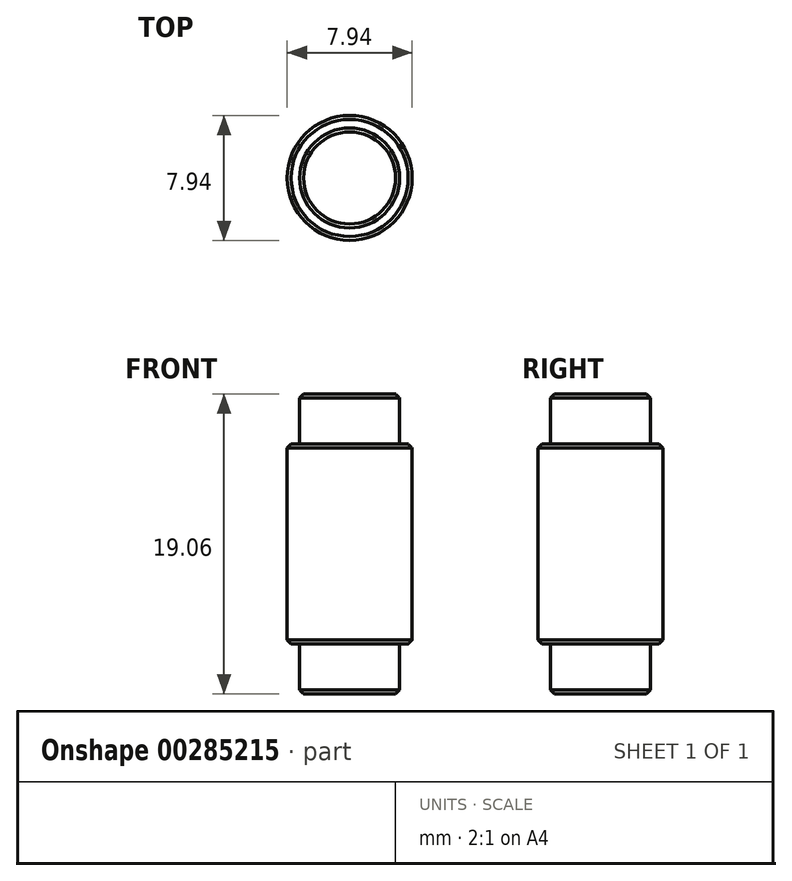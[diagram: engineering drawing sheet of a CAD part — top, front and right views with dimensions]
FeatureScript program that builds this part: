
annotation { "Feature Type Name" : "Feature", "Feature Type Description" : "" }
export const myFeature = defineFeature(function(context is Context, id is Id, definition is map)
    precondition{}
    {
        {
            var Q0;
            Q0=qCreatedBy(makeId("Top.planeOp"),FACE);
            var sketch = newSketch(context, id + "F0", { "sketchPlane" : qUnion([Q0])});
            skCircle(sketch, "E0", {"center": v(0, 0) * mm, "radius": 3.97 * mm});
            skSolve(sketch);
        }
        {
            var Q0;
            Q0 = qSketchRegion(id + "F0", true);
            extrude(context, id + "F1", {"entities" : qUnion([Q0]), "depth" : 12.7 * mm});
        }
        {
            var Q0;
            Q0=makeQuery(id+"F1.opExtrude","CAP_FACE",FACE,{"disambiguationData":[OSD([sQuery(id+"F0.wireOp",EDGE,"E0")])],"isStart":false});
            var sketch = newSketch(context, id + "F2", { "sketchPlane" : qUnion([Q0])});
            skCircle(sketch, "E1", {"center": v(0, 0) * mm, "radius": 3.18 * mm});
            skSolve(sketch);
        }
        {
            var Q0;
            Q0=makeQuery(id+"F2.imprint","IMPRINT",FACE,{"disambiguationData":[TD([[makeQuery(id+"F2.imprint","IMPRINT",EDGE,{"derivedFrom":sQuery(id+"F2.wireOp",EDGE,"E1")}),1.0]])]});
            extrude(context, id + "F3", {"entities" : qUnion([Q0]), "operationType" : NewBodyOperationType.ADD, "depth" : 3.17 * mm});
        }
        {
            var Q0;
            Q0=makeQuery(id+"F1.opExtrude","CAP_FACE",FACE,{"disambiguationData":[OSD([sQuery(id+"F0.wireOp",EDGE,"E0")])],"isStart":true});
            var sketch = newSketch(context, id + "F4", { "sketchPlane" : qUnion([Q0])});
            skCircle(sketch, "E2", {"center": v(0, 0) * mm, "radius": 3.18 * mm});
            skSolve(sketch);
        }
        {
            var Q0;
            Q0=makeQuery(id+"F4.imprint","IMPRINT",FACE,{"disambiguationData":[TD([[makeQuery(id+"F4.imprint","IMPRINT",EDGE,{"derivedFrom":sQuery(id+"F4.wireOp",EDGE,"E2")}),1.0]])]});
            extrude(context, id + "F5", {"entities" : qUnion([Q0]), "operationType" : NewBodyOperationType.ADD, "depth" : 3.17 * mm});
        }
        {
            var Q0;
            Q0=makeQuery(id+"F3.opExtrude","CAP_EDGE",EDGE,{"disambiguationData":[OSD([sQuery(id+"F2.wireOp",EDGE,"E1")])],"isStart":false});
            var Q1;
            Q1=makeQuery(id+"F1.opExtrude","CAP_EDGE",EDGE,{"disambiguationData":[OSD([sQuery(id+"F0.wireOp",EDGE,"E0")])],"isStart":false});
            var Q2;
            Q2=makeQuery(id+"F5.opExtrude","CAP_EDGE",EDGE,{"disambiguationData":[OSD([sQuery(id+"F4.wireOp",EDGE,"E2")])],"isStart":false});
            var Q3;
            Q3=makeQuery(id+"F1.opExtrude","CAP_EDGE",EDGE,{"disambiguationData":[OSD([sQuery(id+"F0.wireOp",EDGE,"E0")])],"isStart":true});
            chamfer(context, id + "F6", {"entities" : qUnion([Q0, Q1, Q2, Q3]), "width" : 0.25 * mm, "tangentPropagation" : true});
        }
    });
